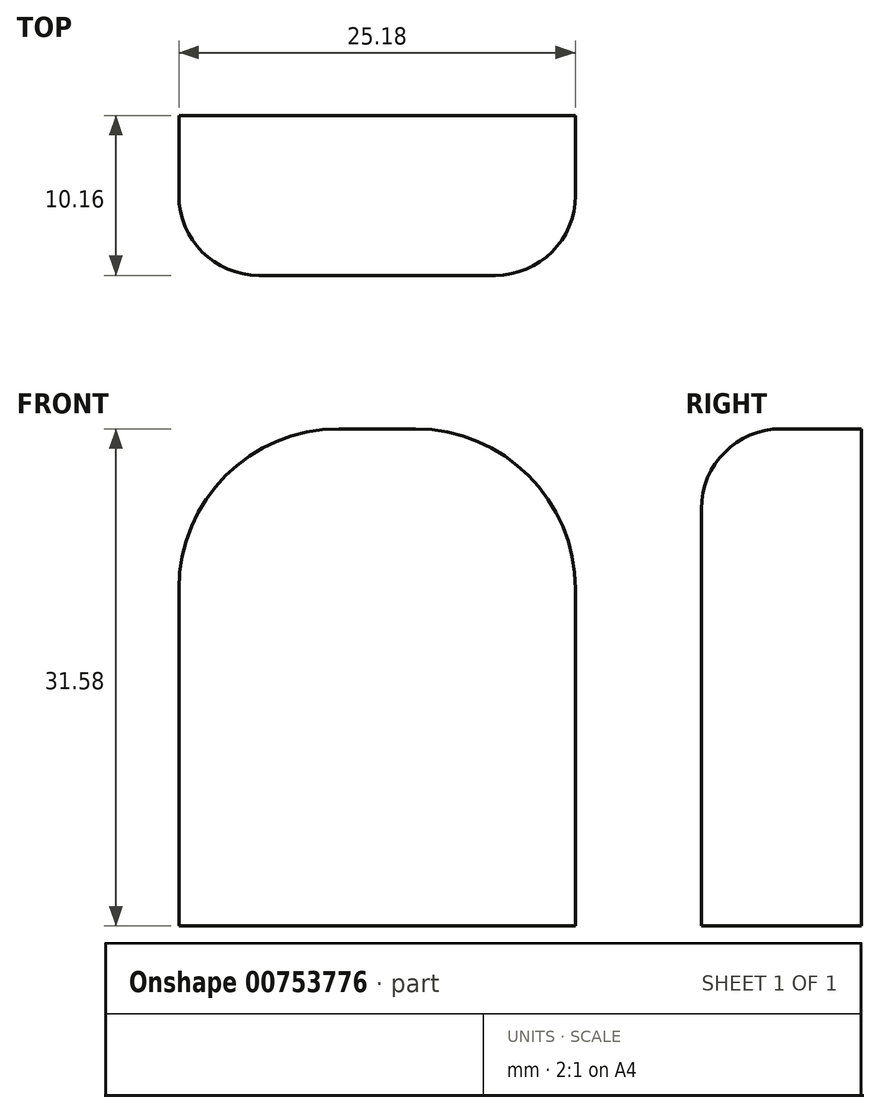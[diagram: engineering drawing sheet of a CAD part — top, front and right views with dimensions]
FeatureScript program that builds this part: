
annotation { "Feature Type Name" : "Feature", "Feature Type Description" : "" }
export const myFeature = defineFeature(function(context is Context, id is Id, definition is map)
    precondition{}
    {
        {
            var Q0;
            Q0=qCreatedBy(makeId("Front.planeOp"),FACE);
            var sketch = newSketch(context, id + "F0", { "sketchPlane" : qUnion([Q0])});
            skLineSegment(sketch, "E0.bottom", {"start": v(12.6, -15.8) * mm, "end": v(-12.6, -15.8) * mm});
            skLineSegment(sketch, "E0.top", {"start": v(2.43, 15.8) * mm, "end": v(-2.43, 15.8) * mm});
            skLineSegment(sketch, "E0.left", {"start": v(12.6, -15.8) * mm, "end": v(12.6, 5.63) * mm});
            skLineSegment(sketch, "E0.right", {"start": v(-12.6, -15.8) * mm, "end": v(-12.6, 5.63) * mm});
            skPoint(sketch, "E0.middle", {"position": v(0, 0) * mm});
            skPoint(sketch, "E1.visualSharp", {"position": v(-12.6, 15.8) * mm});
            skArc(sketch, "E1.filletArc", {"start": v(-2.43, 15.8) * mm, "mid": v(-9.62, 12.82) * mm, "end": v(-12.6, 5.63) * mm});
            skPoint(sketch, "E2.visualSharp", {"position": v(12.6, 15.8) * mm});
            skArc(sketch, "E2.filletArc", {"start": v(12.6, 5.63) * mm, "mid": v(9.62, 12.82) * mm, "end": v(2.43, 15.8) * mm});
            skSolve(sketch);
        }
        {
            var Q0;
            Q0=qSketchRegion(id+"F0",true);
            extrude(context, id + "F1", {"entities" : qUnion([Q0]), "depth" : 10.16 * mm, "offsetDistance" : 25.4 * mm});
        }
        {
            var Q0;
            Q0=makeQuery(id+"F1.opExtrude","CAP_EDGE",EDGE,{"disambiguationData":[OSD([sQuery(id+"F0.wireOp",EDGE,"E2.filletArc")])],"isStart":false});
            var Q1;
            Q1=makeQuery(id+"F1.opExtrude","CAP_EDGE",EDGE,{"disambiguationData":[OSD([sQuery(id+"F0.wireOp",EDGE,"E0.left")])],"isStart":false});
            fillet(context, id + "F2", {"entities" : qUnion([Q0, Q1]), "radius" : 5.08 * mm, "tangentPropagation" : true, "allowEdgeOverflow" : false});
        }
    });
